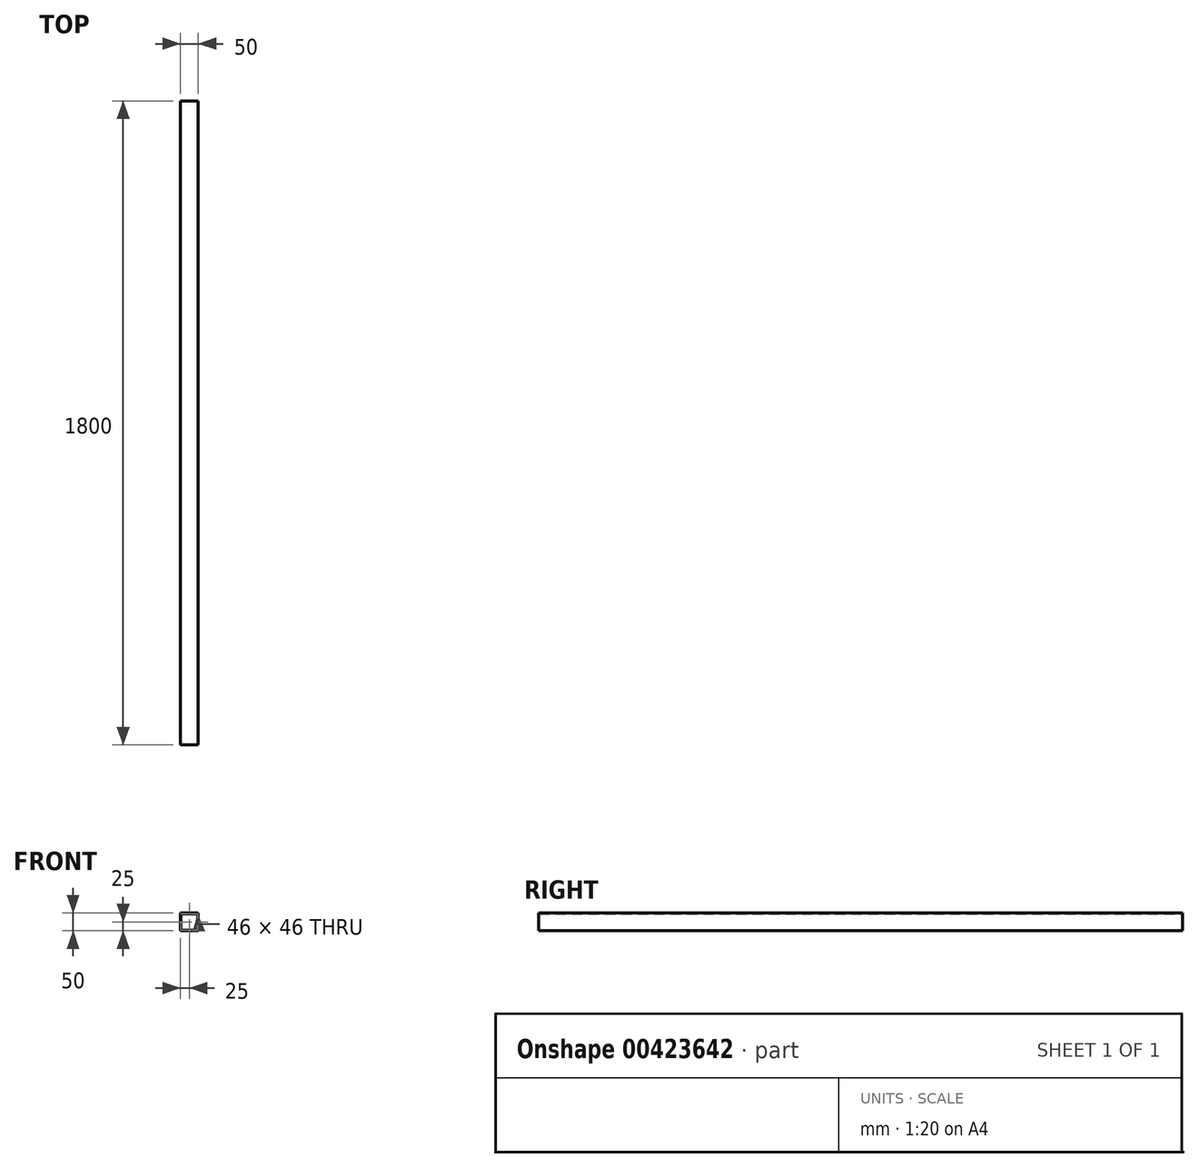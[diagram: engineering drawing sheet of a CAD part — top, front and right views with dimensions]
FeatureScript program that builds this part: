
annotation { "Feature Type Name" : "Feature", "Feature Type Description" : "" }
export const myFeature = defineFeature(function(context is Context, id is Id, definition is map)
    precondition{}
    {
        {
            var Q0;
            Q0=qCreatedBy(makeId("Front.planeOp"),FACE);
            var sketch = newSketch(context, id + "F0", { "sketchPlane" : qUnion([Q0])});
            skLineSegment(sketch, "E0.bottom", {"start": v(0, 0) * mm, "end": v(-50, 0) * mm});
            skLineSegment(sketch, "E0.top", {"start": v(0, 50) * mm, "end": v(-50, 50) * mm});
            skLineSegment(sketch, "E0.left", {"start": v(0, 0) * mm, "end": v(0, 50) * mm});
            skLineSegment(sketch, "E0.right", {"start": v(-50, 0) * mm, "end": v(-50, 50) * mm});
            skLineSegment(sketch, "E1.0", {"start": v(-2, 48) * mm, "end": v(-48, 48) * mm});
            skLineSegment(sketch, "E1.1", {"start": v(-2, 2) * mm, "end": v(-2, 48) * mm});
            skLineSegment(sketch, "E1.2", {"start": v(-2, 2) * mm, "end": v(-48, 2) * mm});
            skLineSegment(sketch, "E1.3", {"start": v(-48, 2) * mm, "end": v(-48, 48) * mm});
            skSolve(sketch);
        }
        {
            var Q0;
            Q0=makeQuery(id+"F0.imprint","IMPRINT",FACE,{"disambiguationData":[TD([[makeQuery(id+"F0.imprint","IMPRINT",EDGE,{"derivedFrom":sQuery(id+"F0.wireOp",EDGE,"E0.bottom")}),-1.0]])]});
            extrude(context, id + "F1", {"entities" : qUnion([Q0]), "depth" : 1800 * mm});
        }
    });
